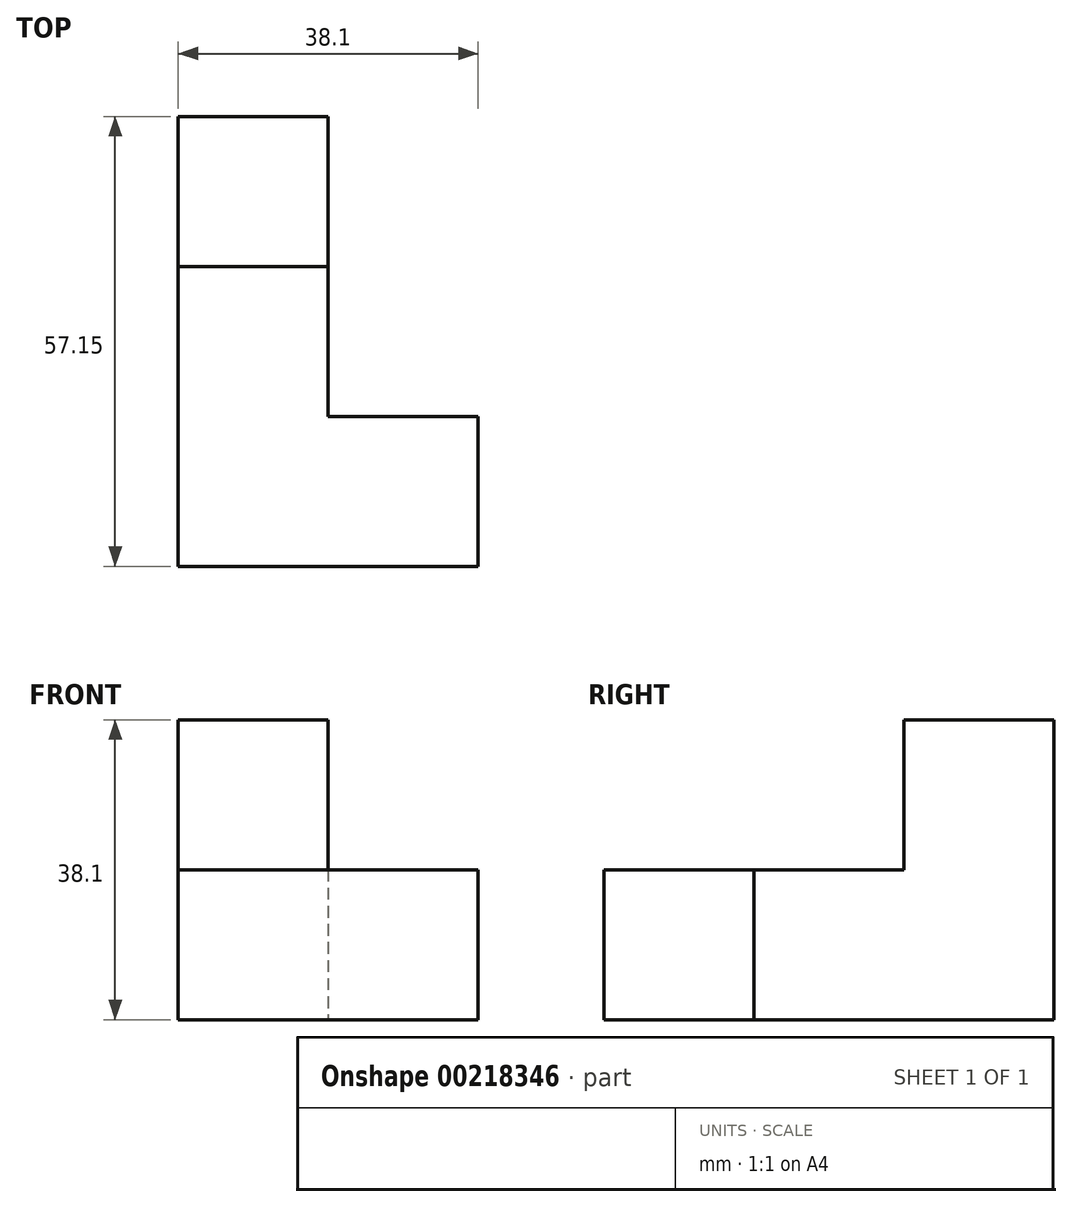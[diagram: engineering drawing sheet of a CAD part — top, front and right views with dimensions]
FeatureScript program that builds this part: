
annotation { "Feature Type Name" : "Feature", "Feature Type Description" : "" }
export const myFeature = defineFeature(function(context is Context, id is Id, definition is map)
    precondition{}
    {
        {
            var Q0;
            Q0=qCreatedBy(makeId("Front.planeOp"),FACE);
            var sketch = newSketch(context, id + "F0", { "sketchPlane" : qUnion([Q0])});
            skLineSegment(sketch, "E0.bottom", {"start": v(-9.52, 9.53) * mm, "end": v(9.53, 9.53) * mm});
            skLineSegment(sketch, "E0.top", {"start": v(-9.53, -9.52) * mm, "end": v(9.52, -9.52) * mm});
            skLineSegment(sketch, "E0.left", {"start": v(-9.52, 9.53) * mm, "end": v(-9.53, -9.52) * mm});
            skLineSegment(sketch, "E0.right", {"start": v(9.53, 9.53) * mm, "end": v(9.52, -9.52) * mm});
            skPoint(sketch, "E0.middle", {"position": v(0, 0) * mm});
            skSolve(sketch);
        }
        {
            var Q0;
            Q0 = qSketchRegion(id + "F0", true);
            extrude(context, id + "F1", {"entities" : qUnion([Q0]), "endBound" : BoundingType.SYMMETRIC, "depth" : 19.05 * mm});
        }
        {
            var Q0;
            Q0=makeQuery(id+"F1.opExtrude","SWEPT_FACE",FACE,{"disambiguationData":[OSD([sQuery(id+"F0.wireOp",EDGE,"E0.bottom")])]});
            extrude(context, id + "F2", {"entities" : qUnion([Q0]), "operationType" : NewBodyOperationType.ADD, "depth" : 19.05 * mm});
        }
        {
            var Q0;
            {var subQ0=sQuery(id+"F0.wireOp",EDGE,"E0.bottom");Q0=makeQuery(id+"F2.boolean.opBoolean","MERGE",FACE,{"derivedFrom":[makeQuery(id+"F1.opExtrude","CAP_FACE",FACE,{"disambiguationData":[OSD([subQ0,sQuery(id+"F0.wireOp",EDGE,"E0.top"),sQuery(id+"F0.wireOp",EDGE,"E0.left"),sQuery(id+"F0.wireOp",EDGE,"E0.right")])],"isStart":false}),makeQuery(id+"F2.opExtrude","SWEPT_FACE",FACE,{"disambiguationData":[OSD([subQ0]),TDD([makeQuery(id+"F1.opExtrude","CAP_EDGE",EDGE,{"disambiguationData":[OSD([subQ0])],"isStart":false})])]})]});}
            var sketch = newSketch(context, id + "F3", { "sketchPlane" : qUnion([Q0])});
            skLineSegment(sketch, "E1.bottom", {"start": v(9.52, -9.52) * mm, "end": v(-9.52, -9.52) * mm});
            skLineSegment(sketch, "E1.top", {"start": v(9.52, 9.53) * mm, "end": v(-9.52, 9.53) * mm});
            skLineSegment(sketch, "E1.left", {"start": v(9.52, -9.52) * mm, "end": v(9.52, 9.53) * mm});
            skLineSegment(sketch, "E1.right", {"start": v(-9.52, -9.52) * mm, "end": v(-9.52, 9.53) * mm});
            skSolve(sketch);
        }
        {
            var Q0;
            Q0=makeQuery(id+"F3.imprint","IMPRINT",FACE,{"disambiguationData":[TD([[makeQuery(id+"F3.imprint","IMPRINT",EDGE,{"derivedFrom":sQuery(id+"F3.wireOp",EDGE,"E1.bottom")}),1.0]])]});
            extrude(context, id + "F4", {"entities" : qUnion([Q0]), "operationType" : NewBodyOperationType.ADD, "depth" : 38.1 * mm});
        }
        {
            var Q0;
            {var subQ0=sQuery(id+"F0.wireOp",EDGE,"E0.right");Q0=makeQuery(id+"F4.boolean.opBoolean","MERGE",FACE,{"derivedFrom":[makeQuery(id+"F2.boolean.opBoolean","MERGE",FACE,{"derivedFrom":[makeQuery(id+"F1.opExtrude","SWEPT_FACE",FACE,{"disambiguationData":[OSD([subQ0])]}),makeQuery(id+"F2.opExtrude","SWEPT_FACE",FACE,{"disambiguationData":[OSD([sQuery(id+"F0.wireOp",EDGE,"E0.bottom"),subQ0])]})]}),makeQuery(id+"F4.opExtrude","SWEPT_FACE",FACE,{"disambiguationData":[OSD([sQuery(id+"F3.wireOp",EDGE,"E1.left")])]})]});}
            var sketch = newSketch(context, id + "F5", { "sketchPlane" : qUnion([Q0])});
            skLineSegment(sketch, "E2.bottom", {"start": v(-47.62, 9.53) * mm, "end": v(-28.57, 9.53) * mm});
            skLineSegment(sketch, "E2.top", {"start": v(-47.62, -9.52) * mm, "end": v(-28.57, -9.52) * mm});
            skLineSegment(sketch, "E2.left", {"start": v(-47.62, 9.53) * mm, "end": v(-47.62, -9.52) * mm});
            skLineSegment(sketch, "E2.right", {"start": v(-28.57, 9.53) * mm, "end": v(-28.57, -9.52) * mm});
            skSolve(sketch);
        }
        {
            var Q0;
            Q0=makeQuery(id+"F5.imprint","IMPRINT",FACE,{"disambiguationData":[TD([[makeQuery(id+"F5.imprint","IMPRINT",EDGE,{"derivedFrom":sQuery(id+"F5.wireOp",EDGE,"E2.bottom")}),-1.0]])]});
            extrude(context, id + "F6", {"entities" : qUnion([Q0]), "operationType" : NewBodyOperationType.ADD, "depth" : 19.05 * mm});
        }
    });
